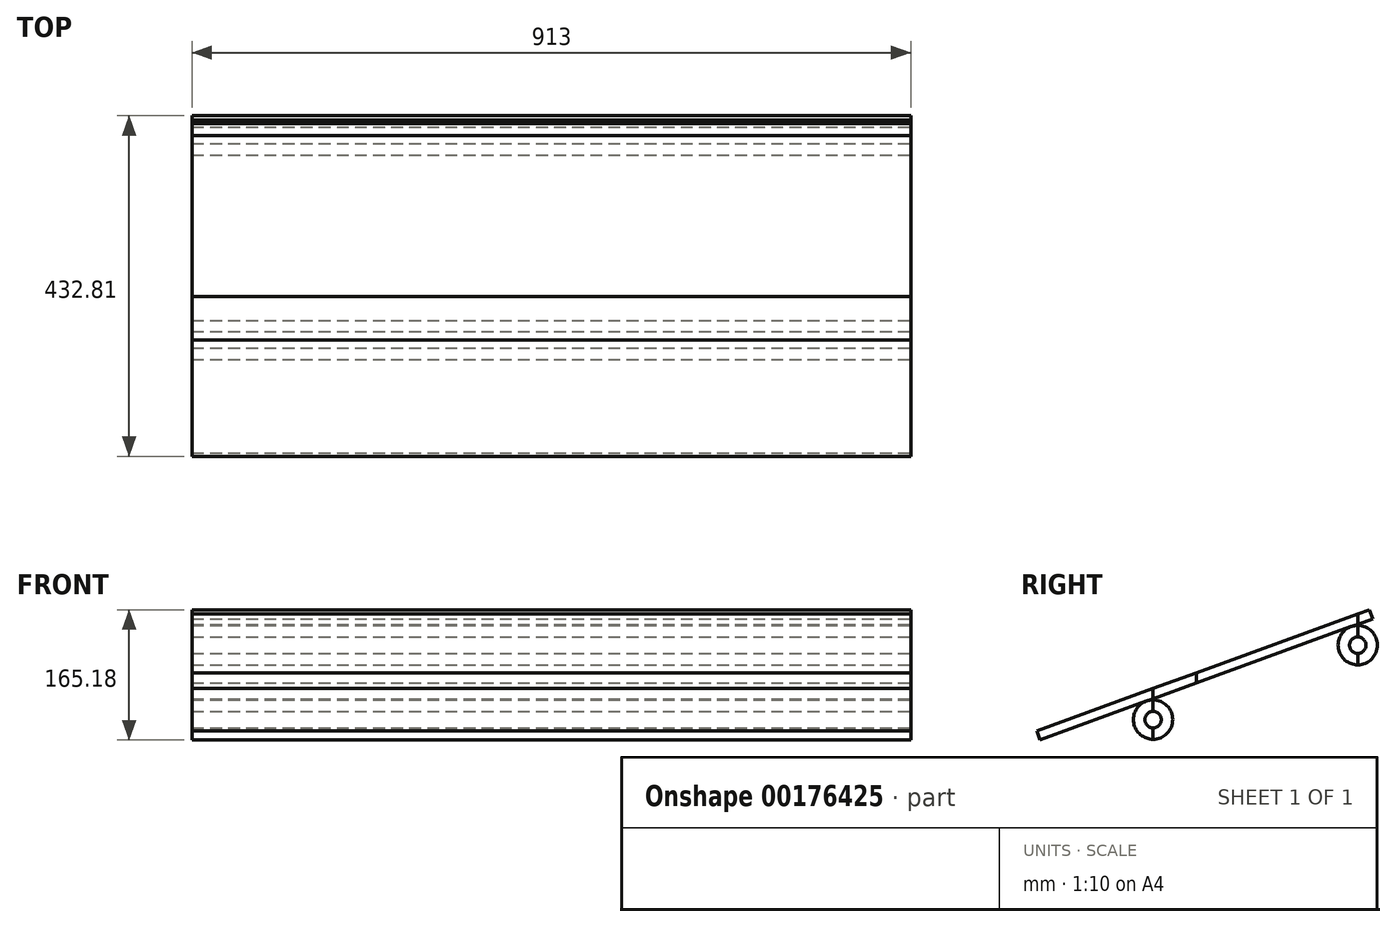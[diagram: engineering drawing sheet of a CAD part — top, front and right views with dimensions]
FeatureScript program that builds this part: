
annotation { "Feature Type Name" : "Feature", "Feature Type Description" : "" }
export const myFeature = defineFeature(function(context is Context, id is Id, definition is map)
    precondition{}
    {
        {
            var Q0;
            Q0=qCreatedBy(makeId("Right.planeOp"),FACE);
            var sketch = newSketch(context, id + "F0", { "sketchPlane" : qUnion([Q0])});
            skLineSegment(sketch, "E0", {"start": v(5.94, 629.26) * mm, "end": v(5.94, -262.67) * mm});
            skLineSegment(sketch, "E1", {"start": v(-137.77, -115.06) * mm, "end": v(285.1, 38.85) * mm});
            skLineSegment(sketch, "E2", {"start": v(-141.87, -103.79) * mm, "end": v(280.99, 50.12) * mm});
            skPoint(sketch, "E3.orphan", {"position": v(5.94, -62.76) * mm});
            skPoint(sketch, "E4", {"position": v(5.94, -107.14) * mm});
            skPoint(sketch, "E5", {"position": v(5.94, -89.36) * mm});
            skLineSegment(sketch, "E6", {"start": v(60.94, 954.25) * mm, "end": v(60.94, -413.84) * mm});
            skPoint(sketch, "E7", {"position": v(60.94, -42.74) * mm});
            skPoint(sketch, "E8", {"position": v(60.94, 629.26) * mm});
            skLineSegment(sketch, "E9", {"start": v(265.94, -99.78) * mm, "end": v(265.94, 134.76) * mm});
            skCircle(sketch, "E10", {"center": v(5.94, -89.36) * mm, "radius": 25 * mm});
            skCircle(sketch, "E11", {"center": v(265.94, 5.27) * mm, "radius": 25 * mm});
            skLineSegment(sketch, "E12", {"start": v(-141.87, -103.79) * mm, "end": v(-137.77, -115.06) * mm});
            skLineSegment(sketch, "E13", {"start": v(280.99, 50.12) * mm, "end": v(285.1, 38.85) * mm});
            skCircle(sketch, "E14", {"center": v(5.94, -89.36) * mm, "radius": 10.5 * mm});
            skCircle(sketch, "E15", {"center": v(265.94, 5.27) * mm, "radius": 10.5 * mm});
            skSolve(sketch);
        }
        {
            var Q0;
            {var subQ0=sQuery(id+"F0.wireOp",EDGE,"E10");var subQ1=sQuery(id+"F0.wireOp",EDGE,"E0");var subQ2=makeQuery(id+"F0.imprint","INTERSECT",VERTEX,{"disambiguationData":[OD(0.0)],"derivedFrom":[subQ1,subQ0]});Q0=makeQuery(id+"F0.imprint","IMPRINT",FACE,{"disambiguationData":[TD([[makeQuery(id+"F0.imprint","IMPRINT",EDGE,{"disambiguationData":[TD([[subQ2,1.0]])],"derivedFrom":subQ1}),1.0]])]});}
            var Q1;
            {var subQ0=sQuery(id+"F0.wireOp",EDGE,"E10");var subQ1=sQuery(id+"F0.wireOp",EDGE,"E0");var subQ2=makeQuery(id+"F0.imprint","INTERSECT",VERTEX,{"disambiguationData":[OD(0.0)],"derivedFrom":[subQ1,subQ0]});Q1=makeQuery(id+"F0.imprint","IMPRINT",FACE,{"disambiguationData":[TD([[makeQuery(id+"F0.imprint","IMPRINT",EDGE,{"disambiguationData":[TD([[subQ2,1.0]])],"derivedFrom":subQ1}),-1.0]])]});}
            var Q2;
            {var subQ0=sQuery(id+"F0.wireOp",EDGE,"E11");var subQ1=sQuery(id+"F0.wireOp",EDGE,"E9");var subQ2=makeQuery(id+"F0.imprint","INTERSECT",VERTEX,{"disambiguationData":[OD(0.0)],"derivedFrom":[subQ1,subQ0]});Q2=makeQuery(id+"F0.imprint","IMPRINT",FACE,{"disambiguationData":[TD([[makeQuery(id+"F0.imprint","IMPRINT",EDGE,{"disambiguationData":[TD([[subQ2,-1.0]])],"derivedFrom":subQ1}),-1.0]])]});}
            var Q3;
            {var subQ0=sQuery(id+"F0.wireOp",EDGE,"E11");var subQ1=sQuery(id+"F0.wireOp",EDGE,"E9");var subQ2=makeQuery(id+"F0.imprint","INTERSECT",VERTEX,{"disambiguationData":[OD(0.0)],"derivedFrom":[subQ1,subQ0]});Q3=makeQuery(id+"F0.imprint","IMPRINT",FACE,{"disambiguationData":[TD([[makeQuery(id+"F0.imprint","IMPRINT",EDGE,{"disambiguationData":[TD([[subQ2,-1.0]])],"derivedFrom":subQ1}),1.0]])]});}
            var Q4;
            {var subQ0=sQuery(id+"F0.wireOp",EDGE,"E6");var subQ1=sQuery(id+"F0.wireOp",EDGE,"E1");var subQ2=makeQuery(id+"F0.imprint","INTERSECT",VERTEX,{"derivedFrom":[subQ1,subQ0]});Q4=makeQuery(id+"F0.imprint","IMPRINT",FACE,{"disambiguationData":[TD([[makeQuery(id+"F0.imprint","IMPRINT",EDGE,{"disambiguationData":[TD([[subQ2,-1.0]])],"derivedFrom":subQ1}),1.0]])]});}
            var Q5;
            {var subQ0=sQuery(id+"F0.wireOp",EDGE,"E2");var subQ1=sQuery(id+"F0.wireOp",EDGE,"E0");var subQ2=makeQuery(id+"F0.imprint","INTERSECT",VERTEX,{"derivedFrom":[subQ1,subQ0]});Q5=makeQuery(id+"F0.imprint","IMPRINT",FACE,{"disambiguationData":[TD([[makeQuery(id+"F0.imprint","IMPRINT",EDGE,{"disambiguationData":[TD([[subQ2,-1.0]])],"derivedFrom":subQ1}),1.0]])]});}
            var Q6;
            {var subQ0=sQuery(id+"F0.wireOp",EDGE,"E12");Q6=makeQuery(id+"F0.imprint","IMPRINT",FACE,{"disambiguationData":[TD([[makeQuery(id+"F0.imprint","IMPRINT",EDGE,{"derivedFrom":subQ0}),1.0]])]});}
            var Q7;
            {var subQ0=sQuery(id+"F0.wireOp",EDGE,"E13");Q7=makeQuery(id+"F0.imprint","IMPRINT",FACE,{"disambiguationData":[TD([[makeQuery(id+"F0.imprint","IMPRINT",EDGE,{"derivedFrom":subQ0}),-1.0]])]});}
            extrude(context, id + "F1", {"entities" : qUnion([Q0, Q1, Q2, Q3, Q4, Q5, Q6, Q7]), "oppositeDirection" : true, "depth" : 913 * mm});
        }
    });
